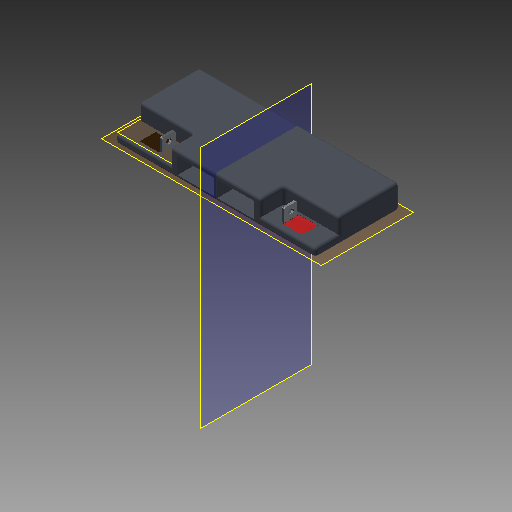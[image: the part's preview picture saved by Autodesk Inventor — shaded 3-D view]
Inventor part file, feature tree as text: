
AUTODESK INVENTOR PART (.ipt)
format: ipt  version: 2018 (Build 220112000, 112)  size: 375,808 bytes
history: native  units: mm (DEFAULTED — no unit token found)
features: sketch x10, extrude x9, fillet x5, plane x5, mirror x3, split x3, hole x1
ambient origin geometry x8: Origin, YZ Plane, XZ Plane, XY Plane, X Axis, Y Axis, Z Axis, Center Point
bodies: Solid1 (feature_tree)
feature tree (36):
  extrude  "Extrusion1"  Depth=74.422mm
  extrude  "Extrusion2"  Depth=139.7mm TaperAngle=0.0deg
  extrude  "Extrusion3"  Depth=21.336mm
  fillet  "Fillet1"  Radius=14.224mm
  fillet  "Fillet3"  Radius=2.54mm
  fillet  "Fillet4"  Radius=2.54mm
  extrude  "Extrusion4"  Depth=0.254mm TaperAngle=0.0deg
  extrude  "Extrusion5"  Depth=12.7mm TaperAngle=0.0deg
  extrude  "Extrusion6"  Depth=12.7mm TaperAngle=0.0deg
  plane  "Work Plane1"
  mirror  "Mirror1"
  mirror  "Mirror2"
  extrude  "Extrusion7"  Depth=20.32mm
  extrude  "Extrusion8"  Depth=19.558mm TaperAngle=0.0deg
  plane  "Work Plane2"
  fillet  "Fillet5"  Radius=33.02mm
  plane  "Work Plane3"
  extrude  "Extrusion9"  Depth=19.05mm TaperAngle=0.0deg
  hole  "Hole1"  [1 undecoded]
  fillet  "Fillet6"  Radius=56.261mm
  mirror  "Mirror3"
  plane  "Work Plane4"
  split  "Split2"
  plane  "Work Plane6"
  split  "Split3"
  split  "Split4"
  sketch  "Sketch1"  dims[d0=179.578mm d1=74.422mm]
  sketch  "Sketch2"  dims[d2=139.7mm d3=0.0mm d4=21.082mm d5=0.0mm]
  sketch  "Sketch3"  dims[d6=49.276mm d7=21.336mm d8=14.224mm d9=0.0mm d10=2.54mm d12=2.54mm]
  sketch  "Sketch4"  dims[d13=2.54mm d14=0.254mm d15=0.0mm]
  sketch  "Sketch5"  dims[d16=1.524mm d17=12.7mm d18=0.0mm]
  sketch  "Sketch6"  dims[d19=5.08mm d20=12.7mm d21=0.0mm]
  sketch  "Sketch7"  dims[d22=20.32mm d23=20.32mm]
  sketch  "Sketch8"  dims[d24=63.5mm d25=19.558mm d26=0.0mm d27=33.02mm]
  sketch  "Sketch9"  dims[d28=3.048mm d29=19.05mm d30=0.0mm]
  sketch  "Sketch10"  dims[d31=181.102mm d32=-127.0mm d34=1.27mm d35=56.261mm d36=11.9888mm d37=11.5062mm d38=2.0066mm d39=0.0mm d40=5.4864mm d41=5.4864mm d42=19.05mm d43=9.525mm d44=6.35mm d45=14.3117mm d46=25.4mm d47=20.594885mm d48=1.27mm d49=14.986mm d50=90.0deg d51=0.0mm]
note: 1 required parameter value undecoded (feature->parameter linkage not recoverable at this tier; creation-order binding heuristic only, values carry confidence <= 0.55)
